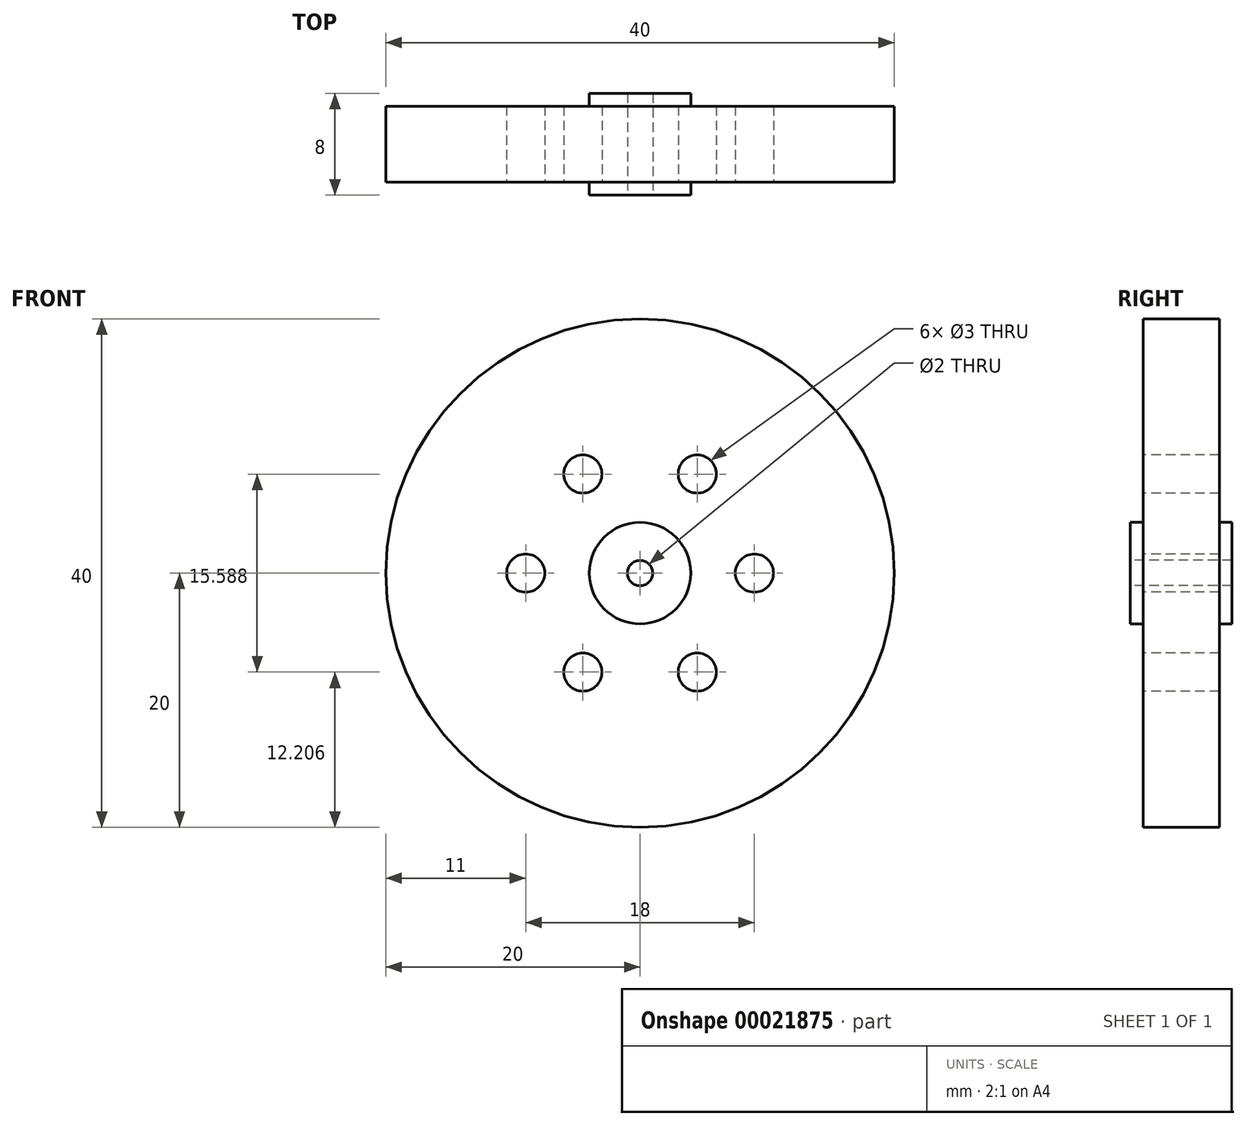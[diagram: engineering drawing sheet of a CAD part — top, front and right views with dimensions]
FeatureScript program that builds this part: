
annotation { "Feature Type Name" : "Feature", "Feature Type Description" : "" }
export const myFeature = defineFeature(function(context is Context, id is Id, definition is map)
    precondition{}
    {
        {
            var Q0;
            Q0=qCreatedBy(makeId("Front.planeOp"),FACE);
            var sketch = newSketch(context, id + "F0", { "sketchPlane" : qUnion([Q0])});
            skCircle(sketch, "E0", {"center": v(0, 0) * mm, "radius": 20 * mm});
            skSolve(sketch);
        }
        {
            var Q0;
            Q0=makeQuery(id+"F0.imprint","IMPRINT",FACE,{"disambiguationData":[TD([[makeQuery(id+"F0.imprint","IMPRINT",EDGE,{"derivedFrom":sQuery(id+"F0.wireOp",EDGE,"E0")}),1.0]])]});
            extrude(context, id + "F1", {"entities" : qUnion([Q0]), "depth" : 6 * mm});
        }
        {
            var Q0;
            Q0=makeQuery(id+"F1.opExtrude","CAP_FACE",FACE,{"disambiguationData":[OSD([sQuery(id+"F0.wireOp",EDGE,"E0")])],"isStart":false});
            var sketch = newSketch(context, id + "F2", { "sketchPlane" : qUnion([Q0])});
            skCircle(sketch, "E1", {"center": v(0, 0) * mm, "radius": 4 * mm});
            skSolve(sketch);
        }
        {
            var Q0;
            Q0=makeQuery(id+"F2.imprint","IMPRINT",FACE,{"disambiguationData":[TD([[makeQuery(id+"F2.imprint","IMPRINT",EDGE,{"derivedFrom":sQuery(id+"F2.wireOp",EDGE,"E1")}),1.0]])]});
            extrude(context, id + "F3", {"entities" : qUnion([Q0]), "operationType" : NewBodyOperationType.ADD, "depth" : 1 * mm});
        }
        {
            var Q0;
            Q0=makeQuery(id+"F3.opExtrude","CAP_FACE",FACE,{"disambiguationData":[OSD([sQuery(id+"F2.wireOp",EDGE,"E1")])],"isStart":false});
            var sketch = newSketch(context, id + "F4", { "sketchPlane" : qUnion([Q0])});
            skCircle(sketch, "E2", {"center": v(0, 0) * mm, "radius": 1 * mm});
            skSolve(sketch);
        }
        {
            var Q0;
            Q0=makeQuery(id+"F4.imprint","IMPRINT",FACE,{"disambiguationData":[TD([[makeQuery(id+"F4.imprint","IMPRINT",EDGE,{"derivedFrom":sQuery(id+"F4.wireOp",EDGE,"E2")}),1.0]])]});
            extrude(context, id + "F5", {"entities" : qUnion([Q0]), "operationType" : NewBodyOperationType.REMOVE, "oppositeDirection" : true, "depth" : 25.4 * mm});
        }
        {
            var Q0;
            Q0=makeQuery(id+"F1.opExtrude","CAP_FACE",FACE,{"disambiguationData":[OSD([sQuery(id+"F0.wireOp",EDGE,"E0")])],"isStart":true});
            var sketch = newSketch(context, id + "F6", { "sketchPlane" : qUnion([Q0])});
            skCircle(sketch, "E3", {"center": v(0, 0) * mm, "radius": 4 * mm});
            skSolve(sketch);
        }
        {
            var Q0;
            Q0=makeQuery(id+"F6.imprint","IMPRINT",FACE,{"disambiguationData":[TD([[makeQuery(id+"F6.imprint","IMPRINT",EDGE,{"derivedFrom":sQuery(id+"F6.wireOp",EDGE,"E3")}),1.0]])]});
            extrude(context, id + "F7", {"entities" : qUnion([Q0]), "operationType" : NewBodyOperationType.ADD, "depth" : 1 * mm});
        }
        {
            var Q0;
            Q0=makeQuery(id+"F1.opExtrude","CAP_FACE",FACE,{"disambiguationData":[OSD([sQuery(id+"F0.wireOp",EDGE,"E0")])],"isStart":false});
            var sketch = newSketch(context, id + "F8", { "sketchPlane" : qUnion([Q0])});
            skCircle(sketch, "E4", {"center": v(9, 0) * mm, "radius": 1.5 * mm});
            skCircle(sketch, "E5.1.0", {"center": v(4.5, 7.8) * mm, "radius": 1.5 * mm});
            skCircle(sketch, "E5.2.0", {"center": v(-4.5, 7.8) * mm, "radius": 1.5 * mm});
            skCircle(sketch, "E5.3.0", {"center": v(-9, 0) * mm, "radius": 1.5 * mm});
            skCircle(sketch, "E5.4.0", {"center": v(-4.5, -7.8) * mm, "radius": 1.5 * mm});
            skCircle(sketch, "E5.5.0", {"center": v(4.5, -7.8) * mm, "radius": 1.5 * mm});
            skPoint(sketch, "E5.center", {"position": v(0, 0) * mm});
            skSolve(sketch);
        }
        {
            var Q0;
            Q0=makeQuery(id+"F8.imprint","IMPRINT",FACE,{"disambiguationData":[TD([[makeQuery(id+"F8.imprint","IMPRINT",EDGE,{"derivedFrom":sQuery(id+"F8.wireOp",EDGE,"E5.4.0")}),1.0]])]});
            var Q1;
            Q1=makeQuery(id+"F8.imprint","IMPRINT",FACE,{"disambiguationData":[TD([[makeQuery(id+"F8.imprint","IMPRINT",EDGE,{"derivedFrom":sQuery(id+"F8.wireOp",EDGE,"E5.5.0")}),1.0]])]});
            var Q2;
            Q2=makeQuery(id+"F8.imprint","IMPRINT",FACE,{"disambiguationData":[TD([[makeQuery(id+"F8.imprint","IMPRINT",EDGE,{"derivedFrom":sQuery(id+"F8.wireOp",EDGE,"E5.3.0")}),1.0]])]});
            var Q3;
            Q3=makeQuery(id+"F8.imprint","IMPRINT",FACE,{"disambiguationData":[TD([[makeQuery(id+"F8.imprint","IMPRINT",EDGE,{"derivedFrom":sQuery(id+"F8.wireOp",EDGE,"E5.2.0")}),1.0]])]});
            var Q4;
            Q4=makeQuery(id+"F8.imprint","IMPRINT",FACE,{"disambiguationData":[TD([[makeQuery(id+"F8.imprint","IMPRINT",EDGE,{"derivedFrom":sQuery(id+"F8.wireOp",EDGE,"E5.1.0")}),1.0]])]});
            var Q5;
            Q5=makeQuery(id+"F8.imprint","IMPRINT",FACE,{"disambiguationData":[TD([[makeQuery(id+"F8.imprint","IMPRINT",EDGE,{"derivedFrom":sQuery(id+"F8.wireOp",EDGE,"E4")}),1.0]])]});
            var Q6;
            Q6=sQuery(id+"F8.wireOp",EDGE,"E5.2.0");
            var Q7;
            Q7=sQuery(id+"F8.wireOp",EDGE,"E5.3.0");
            var Q8;
            Q8=sQuery(id+"F8.wireOp",EDGE,"E5.4.0");
            var Q9;
            Q9=sQuery(id+"F8.wireOp",EDGE,"E5.5.0");
            var Q10;
            Q10=sQuery(id+"F8.wireOp",EDGE,"E4");
            var Q11;
            Q11=sQuery(id+"F8.wireOp",EDGE,"E5.1.0");
            extrude(context, id + "F9", {"entities" : qUnion([Q0, Q1, Q2, Q3, Q4, Q5]), "operationType" : NewBodyOperationType.REMOVE, "surfaceEntities" : qUnion([Q6, Q7, Q8, Q9, Q10, Q11]), "endBound" : BoundingType.THROUGH_ALL, "oppositeDirection" : true, "depth" : 25.4 * mm});
        }
        {
            var Q0;
            Q0=makeQuery(id+"F1.opExtrude","SWEPT_BODY",BODY,{"disambiguationData":[OSD([sQuery(id+"F0.wireOp",EDGE,"E0")])]});
            transform(context, id + "F10", {"entities" : qUnion([Q0]), "transformType" : TransformType.TRANSLATION_3D, "dx" : 0 * mm, "dy" : 0 * mm, "dz" : 0 * mm, "makeCopy" : true});
        }
        {
            var Q0;
            Q0=makeQuery(id+"F10.opPattern","COPY",BODY,{"derivedFrom":makeQuery(id+"F1.opExtrude","SWEPT_BODY",BODY,{"disambiguationData":[OSD([sQuery(id+"F0.wireOp",EDGE,"E0")])]}),"instanceName":"1"});
            deleteBodies(context, id + "F11", {"entities" : qUnion([Q0])});
        }
    });
